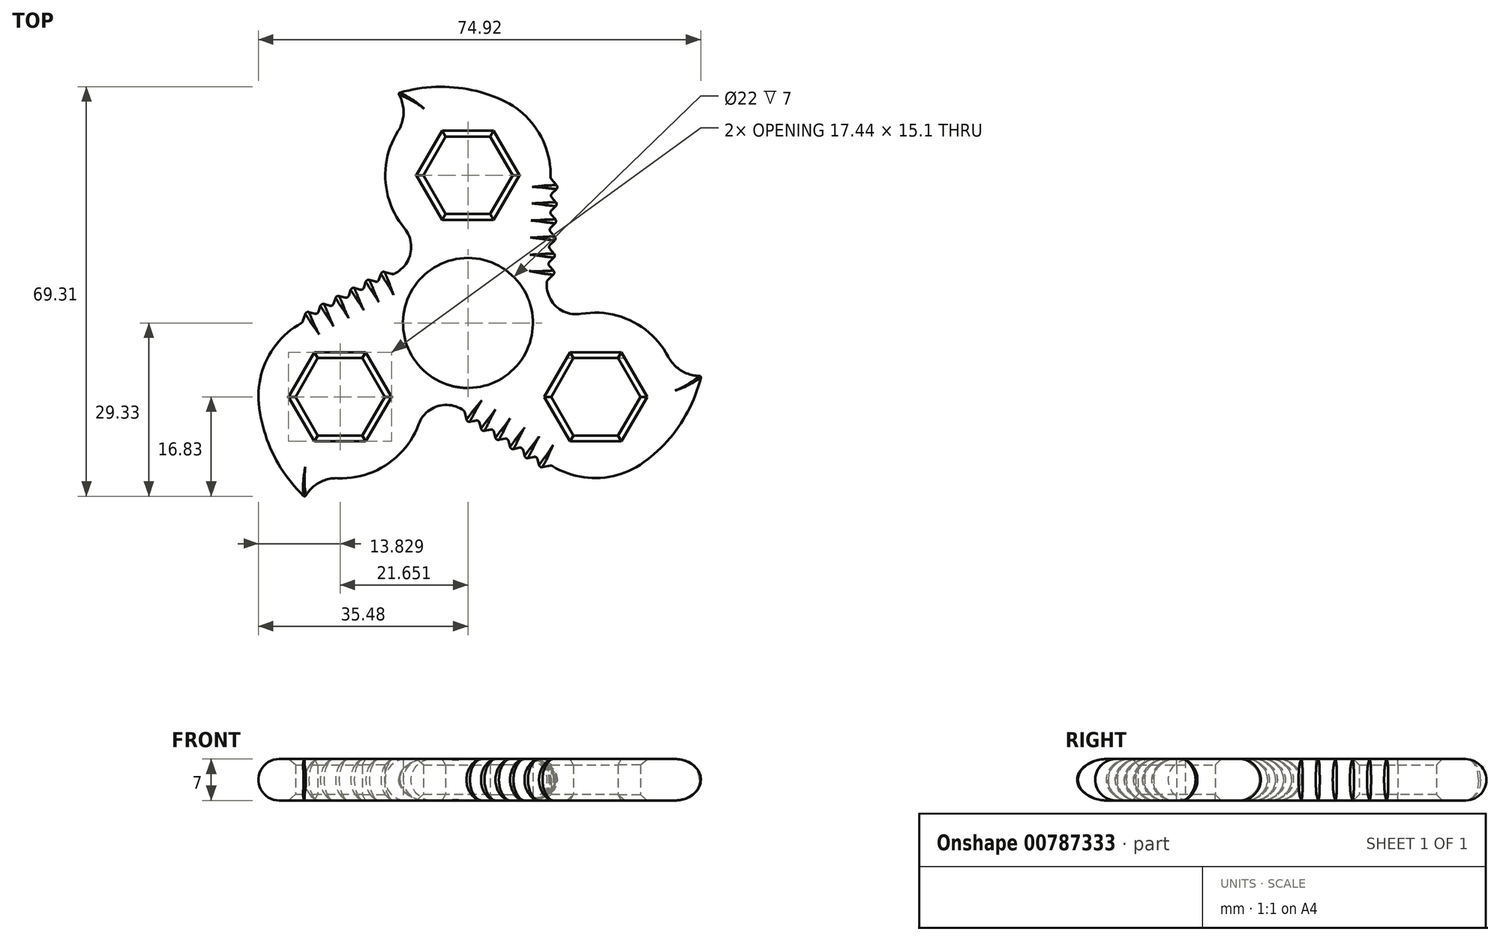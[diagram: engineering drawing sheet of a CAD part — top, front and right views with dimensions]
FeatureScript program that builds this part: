
annotation { "Feature Type Name" : "Feature", "Feature Type Description" : "" }
export const myFeature = defineFeature(function(context is Context, id is Id, definition is map)
    precondition{}
    {
        {
            var Q0;
            Q0=qCreatedBy(makeId("Top.planeOp"),FACE);
            var sketch = newSketch(context, id + "F0", { "sketchPlane" : qUnion([Q0])});
            skCircle(sketch, "E0", {"center": v(0, 0) * mm, "radius": 39 * mm, "construction": true});
            skCircle(sketch, "E1", {"center": v(0, 0) * mm, "radius": 11 * mm});
            skPoint(sketch, "E2.center", {"position": v(0.03, 0) * mm});
            skArc(sketch, "E3", {"start": v(14, 24.5) * mm, "mid": v(11.9, 32.39) * mm, "end": v(5.75, 37.77) * mm});
            skLineSegment(sketch, "E4", {"start": v(13.35, 6.66) * mm, "end": v(13.36, 7.1) * mm});
            skPoint(sketch, "E5.visualSharp", {"position": v(-4.7, 11.81) * mm});
            skArc(sketch, "E5.filletArc", {"start": v(-12.27, 8.44) * mm, "mid": v(-9.7, 11.89) * mm, "end": v(-10.77, 16.05) * mm});
            skPoint(sketch, "E6.visualSharp", {"position": v(13.05, -1.63) * mm});
            skArc(sketch, "E7", {"start": v(5.75, 37.77) * mm, "mid": v(-2.94, 39.93) * mm, "end": v(-11.83, 38.9) * mm});
            skArc(sketch, "E8", {"start": v(-11.83, 32.48) * mm, "mid": v(-10.9, 35.7) * mm, "end": v(-11.83, 38.9) * mm});
            skArc(sketch, "E9.trimOffspring", {"start": v(-11.83, 32.48) * mm, "mid": v(-13.97, 24.1) * mm, "end": v(-10.77, 16.05) * mm});
            skLineSegment(sketch, "E10", {"start": v(14, 24.5) * mm, "end": v(15.31, 23) * mm});
            skLineSegment(sketch, "E11", {"start": v(15.31, 23) * mm, "end": v(13.89, 21.6) * mm});
            skLineSegment(sketch, "E12.1.0.0", {"start": v(15.2, 20.1) * mm, "end": v(13.78, 18.7) * mm});
            skLineSegment(sketch, "E12.1.0.1", {"start": v(13.89, 21.6) * mm, "end": v(15.2, 20.1) * mm});
            skLineSegment(sketch, "E12.2.0.0", {"start": v(15.1, 17.2) * mm, "end": v(13.68, 15.8) * mm});
            skLineSegment(sketch, "E12.2.0.1", {"start": v(13.78, 18.7) * mm, "end": v(15.1, 17.2) * mm});
            skLineSegment(sketch, "E12.3.0.0", {"start": v(15, 14.3) * mm, "end": v(13.57, 12.9) * mm});
            skLineSegment(sketch, "E12.3.0.1", {"start": v(13.68, 15.8) * mm, "end": v(15, 14.3) * mm});
            skLineSegment(sketch, "E12.4.0.0", {"start": v(14.9, 11.4) * mm, "end": v(13.47, 10) * mm});
            skLineSegment(sketch, "E12.4.0.1", {"start": v(13.57, 12.9) * mm, "end": v(14.9, 11.4) * mm});
            skLineSegment(sketch, "E12.5.0.0", {"start": v(14.79, 8.5) * mm, "end": v(13.36, 7.1) * mm});
            skLineSegment(sketch, "E12.5.0.1", {"start": v(13.47, 10) * mm, "end": v(14.79, 8.5) * mm});
            skArc(sketch, "E13.1.0", {"start": v(-22.04, -26.28) * mm, "mid": v(-25.29, -27.08) * mm, "end": v(-27.6, -29.49) * mm});
            skArc(sketch, "E13.1.1", {"start": v(-1, -14.64) * mm, "mid": v(-5.27, -14.14) * mm, "end": v(-8.35, -17.14) * mm});
            skArc(sketch, "E13.1.2", {"start": v(-22.04, -26.28) * mm, "mid": v(-13.71, -23.93) * mm, "end": v(-8.35, -17.14) * mm});
            skArc(sketch, "E13.1.3", {"start": v(-35.41, -13.7) * mm, "mid": v(-32.94, -22.3) * mm, "end": v(-27.6, -29.49) * mm});
            skArc(sketch, "E13.1.4", {"start": v(-28.04, 0.08) * mm, "mid": v(-33.82, -5.68) * mm, "end": v(-35.41, -13.7) * mm});
            skLineSegment(sketch, "E13.1.6", {"start": v(-28.04, 0.08) * mm, "end": v(-27.4, 1.98) * mm});
            skLineSegment(sketch, "E13.1.7", {"start": v(-27.4, 1.98) * mm, "end": v(-25.47, 1.44) * mm});
            skLineSegment(sketch, "E13.1.8", {"start": v(-25.48, 1.44) * mm, "end": v(-24.84, 3.34) * mm});
            skLineSegment(sketch, "E13.1.9", {"start": v(-24.84, 3.34) * mm, "end": v(-22.91, 2.8) * mm});
            skLineSegment(sketch, "E13.1.10", {"start": v(-22.91, 2.8) * mm, "end": v(-22.28, 4.7) * mm});
            skLineSegment(sketch, "E13.1.11", {"start": v(-22.28, 4.7) * mm, "end": v(-20.35, 4.16) * mm});
            skLineSegment(sketch, "E13.1.12", {"start": v(-20.35, 4.16) * mm, "end": v(-19.71, 6.05) * mm});
            skLineSegment(sketch, "E13.1.13", {"start": v(-19.71, 6.05) * mm, "end": v(-17.79, 5.52) * mm});
            skLineSegment(sketch, "E13.1.14", {"start": v(-17.79, 5.51) * mm, "end": v(-17.15, 7.41) * mm});
            skLineSegment(sketch, "E13.1.15", {"start": v(-17.15, 7.41) * mm, "end": v(-15.23, 6.87) * mm});
            skLineSegment(sketch, "E13.1.16", {"start": v(-15.23, 6.87) * mm, "end": v(-14.59, 8.77) * mm});
            skLineSegment(sketch, "E13.1.17", {"start": v(-14.59, 8.77) * mm, "end": v(-12.66, 8.23) * mm});
            skLineSegment(sketch, "E13.1.18", {"start": v(-12.27, 8.44) * mm, "end": v(-12.66, 8.23) * mm});
            skArc(sketch, "E13.2.0", {"start": v(33.95, -5.74) * mm, "mid": v(36.26, -8.15) * mm, "end": v(39.5, -8.95) * mm});
            skArc(sketch, "E13.2.1", {"start": v(13.35, 6.66) * mm, "mid": v(15.05, 2.72) * mm, "end": v(19.19, 1.55) * mm});
            skArc(sketch, "E13.2.2", {"start": v(33.95, -5.74) * mm, "mid": v(27.75, 0.3) * mm, "end": v(19.19, 1.55) * mm});
            skArc(sketch, "E13.2.3", {"start": v(29.73, -23.6) * mm, "mid": v(35.95, -17.16) * mm, "end": v(39.5, -8.95) * mm});
            skArc(sketch, "E13.2.4", {"start": v(14.12, -24.11) * mm, "mid": v(22, -26.24) * mm, "end": v(29.73, -23.6) * mm});
            skLineSegment(sketch, "E13.2.6", {"start": v(14.12, -24.11) * mm, "end": v(12.16, -24.5) * mm});
            skLineSegment(sketch, "E13.2.7", {"start": v(12.16, -24.5) * mm, "end": v(11.66, -22.57) * mm});
            skLineSegment(sketch, "E13.2.8", {"start": v(11.66, -22.57) * mm, "end": v(9.7, -22.97) * mm});
            skLineSegment(sketch, "E13.2.9", {"start": v(9.7, -22.97) * mm, "end": v(9.2, -21.03) * mm});
            skLineSegment(sketch, "E13.2.10", {"start": v(9.2, -21.03) * mm, "end": v(7.24, -21.43) * mm});
            skLineSegment(sketch, "E13.2.11", {"start": v(7.24, -21.43) * mm, "end": v(6.74, -19.5) * mm});
            skLineSegment(sketch, "E13.2.12", {"start": v(6.75, -19.5) * mm, "end": v(4.79, -19.89) * mm});
            skLineSegment(sketch, "E13.2.13", {"start": v(4.79, -19.89) * mm, "end": v(4.29, -17.95) * mm});
            skLineSegment(sketch, "E13.2.14", {"start": v(4.29, -17.95) * mm, "end": v(2.33, -18.35) * mm});
            skLineSegment(sketch, "E13.2.15", {"start": v(2.33, -18.35) * mm, "end": v(1.83, -16.41) * mm});
            skLineSegment(sketch, "E13.2.16", {"start": v(1.83, -16.41) * mm, "end": v(-0.13, -16.8) * mm});
            skLineSegment(sketch, "E13.2.17", {"start": v(-0.13, -16.8) * mm, "end": v(-0.63, -14.87) * mm});
            skLineSegment(sketch, "E13.2.18", {"start": v(-1, -14.64) * mm, "end": v(-0.63, -14.87) * mm});
            skPoint(sketch, "E13.center", {"position": v(0.02, 0.15) * mm});
            skLineSegment(sketch, "E14.trimOffspring", {"start": v(-25.47, 1.44) * mm, "end": v(-25.48, 1.44) * mm});
            skLineSegment(sketch, "E15.trimOffspring", {"start": v(-22.91, 2.8) * mm, "end": v(-22.91, 2.8) * mm});
            skLineSegment(sketch, "E16.trimOffspring", {"start": v(-20.35, 4.16) * mm, "end": v(-20.35, 4.16) * mm});
            skLineSegment(sketch, "E17.trimOffspring", {"start": v(-17.79, 5.52) * mm, "end": v(-17.79, 5.51) * mm});
            skLineSegment(sketch, "E18.trimOffspring", {"start": v(-15.23, 6.87) * mm, "end": v(-15.23, 6.87) * mm});
            skLineSegment(sketch, "E19.trimOffspring", {"start": v(1.83, -16.41) * mm, "end": v(1.83, -16.41) * mm});
            skLineSegment(sketch, "E20.trimOffspring", {"start": v(4.29, -17.95) * mm, "end": v(4.29, -17.95) * mm});
            skLineSegment(sketch, "E21.trimOffspring", {"start": v(6.74, -19.5) * mm, "end": v(6.75, -19.5) * mm});
            skLineSegment(sketch, "E22.trimOffspring", {"start": v(9.2, -21.03) * mm, "end": v(9.2, -21.03) * mm});
            skLineSegment(sketch, "E23.trimOffspring", {"start": v(11.26, -22.32) * mm, "end": v(11.66, -22.57) * mm});
            skLineSegment(sketch, "E24.trimOffspring", {"start": v(13.47, 10) * mm, "end": v(13.47, 10) * mm});
            skLineSegment(sketch, "E25.trimOffspring", {"start": v(13.57, 12.9) * mm, "end": v(13.57, 12.9) * mm});
            skLineSegment(sketch, "E26.trimOffspring", {"start": v(13.68, 15.8) * mm, "end": v(13.68, 15.8) * mm});
            skLineSegment(sketch, "E27.trimOffspring", {"start": v(13.78, 18.7) * mm, "end": v(13.78, 18.7) * mm});
            skLineSegment(sketch, "E28.trimOffspring", {"start": v(13.78, 18.7) * mm, "end": v(13.78, 18.7) * mm, "construction": true});
            skLineSegment(sketch, "E29.trimOffspring", {"start": v(13.89, 21.6) * mm, "end": v(13.89, 21.6) * mm});
            skCircle(sketch, "E30.cCircle", {"center": v(0, 25) * mm, "radius": 6.55 * mm, "construction": true});
            skLineSegment(sketch, "E30.0", {"start": v(7.56, 25) * mm, "end": v(3.78, 18.45) * mm});
            skLineSegment(sketch, "E30.1", {"start": v(3.78, 18.45) * mm, "end": v(-3.78, 18.45) * mm});
            skLineSegment(sketch, "E30.2", {"start": v(-3.78, 18.45) * mm, "end": v(-7.56, 25) * mm});
            skLineSegment(sketch, "E30.3", {"start": v(-7.56, 25) * mm, "end": v(-3.78, 31.55) * mm});
            skLineSegment(sketch, "E30.4", {"start": v(-3.78, 31.55) * mm, "end": v(3.78, 31.55) * mm});
            skLineSegment(sketch, "E30.5", {"start": v(3.78, 31.55) * mm, "end": v(7.56, 25) * mm});
            skPoint(sketch, "E30.0.midPoint", {"position": v(5.67, 21.72) * mm});
            skLineSegment(sketch, "E31.1.0", {"start": v(-25.43, -19.05) * mm, "end": v(-29.21, -12.5) * mm});
            skPoint(sketch, "E31.1.1", {"position": v(-21.65, -5.95) * mm});
            skLineSegment(sketch, "E31.1.2", {"start": v(-17.87, -19.05) * mm, "end": v(-25.43, -19.05) * mm});
            skLineSegment(sketch, "E31.1.3", {"start": v(-14.09, -12.5) * mm, "end": v(-17.87, -19.05) * mm});
            skLineSegment(sketch, "E31.1.4", {"start": v(-17.87, -5.95) * mm, "end": v(-14.09, -12.5) * mm});
            skLineSegment(sketch, "E31.1.5", {"start": v(-29.21, -12.5) * mm, "end": v(-25.43, -5.95) * mm});
            skCircle(sketch, "E31.1.6", {"center": v(-21.65, -12.5) * mm, "radius": 6.55 * mm, "construction": true});
            skLineSegment(sketch, "E31.1.7", {"start": v(-25.43, -5.95) * mm, "end": v(-17.87, -5.95) * mm});
            skLineSegment(sketch, "E31.2.0", {"start": v(29.21, -12.5) * mm, "end": v(25.43, -19.05) * mm});
            skPoint(sketch, "E31.2.1", {"position": v(15.98, -15.77) * mm});
            skLineSegment(sketch, "E31.2.2", {"start": v(25.43, -5.95) * mm, "end": v(29.21, -12.5) * mm});
            skLineSegment(sketch, "E31.2.3", {"start": v(17.87, -5.95) * mm, "end": v(25.43, -5.95) * mm});
            skLineSegment(sketch, "E31.2.4", {"start": v(14.09, -12.5) * mm, "end": v(17.87, -5.95) * mm});
            skLineSegment(sketch, "E31.2.5", {"start": v(25.43, -19.05) * mm, "end": v(17.87, -19.05) * mm});
            skCircle(sketch, "E31.2.6", {"center": v(21.65, -12.5) * mm, "radius": 6.55 * mm, "construction": true});
            skLineSegment(sketch, "E31.2.7", {"start": v(17.87, -19.05) * mm, "end": v(14.09, -12.5) * mm});
            skSolve(sketch);
        }
        {
            var Q0;
            Q0=qSketchRegion(id+"F0",true);
            extrude(context, id + "F1", {"entities" : qUnion([Q0]), "depth" : 7 * mm, "offsetDistance" : 25 * mm});
        }
        {
            var Q0;
            Q0=makeQuery(id+"F1.opExtrude","SWEPT_EDGE",EDGE,{"disambiguationData":[OSD([sQuery(id+"F0.wireOp",EDGE,"E13.1.17"),sQuery(id+"F0.wireOp",EDGE,"E13.1.18")])]});
            var Q1;
            Q1=makeQuery(id+"F1.opExtrude","SWEPT_EDGE",EDGE,{"disambiguationData":[OSD([sQuery(id+"F0.wireOp",EDGE,"E13.1.16"),sQuery(id+"F0.wireOp",EDGE,"E13.1.17")])]});
            var Q2;
            Q2=makeQuery(id+"F1.opExtrude","SWEPT_EDGE",EDGE,{"disambiguationData":[OSD([sQuery(id+"F0.wireOp",EDGE,"E13.1.15"),sQuery(id+"F0.wireOp",EDGE,"E13.1.16")])]});
            var Q3;
            Q3=makeQuery(id+"F1.opExtrude","SWEPT_EDGE",EDGE,{"disambiguationData":[OSD([sQuery(id+"F0.wireOp",EDGE,"E13.1.14"),sQuery(id+"F0.wireOp",EDGE,"E13.1.15")])]});
            var Q4;
            Q4=makeQuery(id+"F1.opExtrude","SWEPT_EDGE",EDGE,{"disambiguationData":[OSD([sQuery(id+"F0.wireOp",EDGE,"E13.1.13"),sQuery(id+"F0.wireOp",EDGE,"E13.1.14")])]});
            var Q5;
            Q5=makeQuery(id+"F1.opExtrude","SWEPT_EDGE",EDGE,{"disambiguationData":[OSD([sQuery(id+"F0.wireOp",EDGE,"E13.1.12"),sQuery(id+"F0.wireOp",EDGE,"E13.1.13")])]});
            var Q6;
            Q6=makeQuery(id+"F1.opExtrude","SWEPT_EDGE",EDGE,{"disambiguationData":[OSD([sQuery(id+"F0.wireOp",EDGE,"E13.1.11"),sQuery(id+"F0.wireOp",EDGE,"E13.1.12")])]});
            var Q7;
            Q7=makeQuery(id+"F1.opExtrude","SWEPT_EDGE",EDGE,{"disambiguationData":[OSD([sQuery(id+"F0.wireOp",EDGE,"E13.1.10"),sQuery(id+"F0.wireOp",EDGE,"E13.1.11")])]});
            var Q8;
            Q8=makeQuery(id+"F1.opExtrude","SWEPT_EDGE",EDGE,{"disambiguationData":[OSD([sQuery(id+"F0.wireOp",EDGE,"E13.1.9"),sQuery(id+"F0.wireOp",EDGE,"E13.1.10")])]});
            var Q9;
            Q9=makeQuery(id+"F1.opExtrude","SWEPT_EDGE",EDGE,{"disambiguationData":[OSD([sQuery(id+"F0.wireOp",EDGE,"E13.1.8"),sQuery(id+"F0.wireOp",EDGE,"E13.1.9")])]});
            var Q10;
            Q10=makeQuery(id+"F1.opExtrude","SWEPT_EDGE",EDGE,{"disambiguationData":[OSD([sQuery(id+"F0.wireOp",EDGE,"E13.1.7"),sQuery(id+"F0.wireOp",EDGE,"E13.1.8")])]});
            var Q11;
            Q11=makeQuery(id+"F1.opExtrude","SWEPT_EDGE",EDGE,{"disambiguationData":[OSD([sQuery(id+"F0.wireOp",EDGE,"E13.1.6"),sQuery(id+"F0.wireOp",EDGE,"E13.1.7")])]});
            var Q12;
            Q12=makeQuery(id+"F1.opExtrude","SWEPT_EDGE",EDGE,{"disambiguationData":[OSD([sQuery(id+"F0.wireOp",EDGE,"E13.1.4"),sQuery(id+"F0.wireOp",EDGE,"E13.1.6")])]});
            var Q13;
            Q13=makeQuery(id+"F1.opExtrude","SWEPT_EDGE",EDGE,{"disambiguationData":[OSD([sQuery(id+"F0.wireOp",EDGE,"E13.2.17"),sQuery(id+"F0.wireOp",EDGE,"E13.2.18")])]});
            var Q14;
            Q14=makeQuery(id+"F1.opExtrude","SWEPT_EDGE",EDGE,{"disambiguationData":[OSD([sQuery(id+"F0.wireOp",EDGE,"E13.2.16"),sQuery(id+"F0.wireOp",EDGE,"E13.2.17")])]});
            var Q15;
            Q15=makeQuery(id+"F1.opExtrude","SWEPT_EDGE",EDGE,{"disambiguationData":[OSD([sQuery(id+"F0.wireOp",EDGE,"E13.2.15"),sQuery(id+"F0.wireOp",EDGE,"E13.2.16")])]});
            var Q16;
            Q16=makeQuery(id+"F1.opExtrude","SWEPT_EDGE",EDGE,{"disambiguationData":[OSD([sQuery(id+"F0.wireOp",EDGE,"E13.2.14"),sQuery(id+"F0.wireOp",EDGE,"E13.2.15")])]});
            var Q17;
            Q17=makeQuery(id+"F1.opExtrude","SWEPT_EDGE",EDGE,{"disambiguationData":[OSD([sQuery(id+"F0.wireOp",EDGE,"E13.2.13"),sQuery(id+"F0.wireOp",EDGE,"E13.2.14")])]});
            var Q18;
            Q18=makeQuery(id+"F1.opExtrude","SWEPT_EDGE",EDGE,{"disambiguationData":[OSD([sQuery(id+"F0.wireOp",EDGE,"E13.2.12"),sQuery(id+"F0.wireOp",EDGE,"E13.2.13")])]});
            var Q19;
            Q19=makeQuery(id+"F1.opExtrude","SWEPT_EDGE",EDGE,{"disambiguationData":[OSD([sQuery(id+"F0.wireOp",EDGE,"E13.2.11"),sQuery(id+"F0.wireOp",EDGE,"E13.2.12")])]});
            var Q20;
            Q20=makeQuery(id+"F1.opExtrude","SWEPT_EDGE",EDGE,{"disambiguationData":[OSD([sQuery(id+"F0.wireOp",EDGE,"E13.2.10"),sQuery(id+"F0.wireOp",EDGE,"E13.2.11")])]});
            var Q21;
            Q21=makeQuery(id+"F1.opExtrude","SWEPT_EDGE",EDGE,{"disambiguationData":[OSD([sQuery(id+"F0.wireOp",EDGE,"E13.2.9"),sQuery(id+"F0.wireOp",EDGE,"E13.2.10")])]});
            var Q22;
            Q22=makeQuery(id+"F1.opExtrude","SWEPT_EDGE",EDGE,{"disambiguationData":[OSD([sQuery(id+"F0.wireOp",EDGE,"E13.2.8"),sQuery(id+"F0.wireOp",EDGE,"E13.2.9")])]});
            var Q23;
            Q23=makeQuery(id+"F1.opExtrude","SWEPT_EDGE",EDGE,{"disambiguationData":[OSD([sQuery(id+"F0.wireOp",EDGE,"E13.2.7"),sQuery(id+"F0.wireOp",EDGE,"E13.2.8")])]});
            var Q24;
            Q24=makeQuery(id+"F1.opExtrude","SWEPT_EDGE",EDGE,{"disambiguationData":[OSD([sQuery(id+"F0.wireOp",EDGE,"E13.2.6"),sQuery(id+"F0.wireOp",EDGE,"E13.2.7")])]});
            var Q25;
            Q25=makeQuery(id+"F1.opExtrude","SWEPT_EDGE",EDGE,{"disambiguationData":[OSD([sQuery(id+"F0.wireOp",EDGE,"E13.2.4"),sQuery(id+"F0.wireOp",EDGE,"E13.2.6")])]});
            var Q26;
            Q26=makeQuery(id+"F1.opExtrude","SWEPT_EDGE",EDGE,{"disambiguationData":[OSD([sQuery(id+"F0.wireOp",EDGE,"E3"),sQuery(id+"F0.wireOp",EDGE,"E10")])]});
            var Q27;
            Q27=makeQuery(id+"F1.opExtrude","SWEPT_EDGE",EDGE,{"disambiguationData":[OSD([sQuery(id+"F0.wireOp",EDGE,"E10"),sQuery(id+"F0.wireOp",EDGE,"E11")])]});
            var Q28;
            Q28=makeQuery(id+"F1.opExtrude","SWEPT_EDGE",EDGE,{"disambiguationData":[OSD([sQuery(id+"F0.wireOp",EDGE,"E11"),sQuery(id+"F0.wireOp",EDGE,"E12.1.0.1")])]});
            var Q29;
            Q29=makeQuery(id+"F1.opExtrude","SWEPT_EDGE",EDGE,{"disambiguationData":[OSD([sQuery(id+"F0.wireOp",EDGE,"E12.1.0.0"),sQuery(id+"F0.wireOp",EDGE,"E12.1.0.1")])]});
            var Q30;
            Q30=makeQuery(id+"F1.opExtrude","SWEPT_EDGE",EDGE,{"disambiguationData":[OSD([sQuery(id+"F0.wireOp",EDGE,"E12.1.0.0"),sQuery(id+"F0.wireOp",EDGE,"E12.2.0.1")])]});
            var Q31;
            Q31=makeQuery(id+"F1.opExtrude","SWEPT_EDGE",EDGE,{"disambiguationData":[OSD([sQuery(id+"F0.wireOp",EDGE,"E12.2.0.0"),sQuery(id+"F0.wireOp",EDGE,"E12.2.0.1")])]});
            var Q32;
            Q32=makeQuery(id+"F1.opExtrude","SWEPT_EDGE",EDGE,{"disambiguationData":[OSD([sQuery(id+"F0.wireOp",EDGE,"E12.2.0.0"),sQuery(id+"F0.wireOp",EDGE,"E12.3.0.1")])]});
            var Q33;
            Q33=makeQuery(id+"F1.opExtrude","SWEPT_EDGE",EDGE,{"disambiguationData":[OSD([sQuery(id+"F0.wireOp",EDGE,"E12.3.0.0"),sQuery(id+"F0.wireOp",EDGE,"E12.3.0.1")])]});
            var Q34;
            Q34=makeQuery(id+"F1.opExtrude","SWEPT_EDGE",EDGE,{"disambiguationData":[OSD([sQuery(id+"F0.wireOp",EDGE,"E12.3.0.0"),sQuery(id+"F0.wireOp",EDGE,"E12.4.0.1")])]});
            var Q35;
            Q35=makeQuery(id+"F1.opExtrude","SWEPT_EDGE",EDGE,{"disambiguationData":[OSD([sQuery(id+"F0.wireOp",EDGE,"E12.4.0.0"),sQuery(id+"F0.wireOp",EDGE,"E12.4.0.1")])]});
            var Q36;
            Q36=makeQuery(id+"F1.opExtrude","SWEPT_EDGE",EDGE,{"disambiguationData":[OSD([sQuery(id+"F0.wireOp",EDGE,"E12.4.0.0"),sQuery(id+"F0.wireOp",EDGE,"E12.5.0.1")])]});
            var Q37;
            Q37=makeQuery(id+"F1.opExtrude","SWEPT_EDGE",EDGE,{"disambiguationData":[OSD([sQuery(id+"F0.wireOp",EDGE,"E12.5.0.0"),sQuery(id+"F0.wireOp",EDGE,"E12.5.0.1")])]});
            var Q38;
            Q38=makeQuery(id+"F1.opExtrude","SWEPT_EDGE",EDGE,{"disambiguationData":[OSD([sQuery(id+"F0.wireOp",EDGE,"E4"),sQuery(id+"F0.wireOp",EDGE,"E12.5.0.0")])]});
            fillet(context, id + "F2", {"entities" : qUnion([Q0, Q1, Q2, Q3, Q4, Q5, Q6, Q7, Q8, Q9, Q10, Q11, Q12, Q13, Q14, Q15, Q16, Q17, Q18, Q19, Q20, Q21, Q22, Q23, Q24, Q25, Q26, Q27, Q28, Q29, Q30, Q31, Q32, Q33, Q34, Q35, Q36, Q37, Q38]), "radius" : .5 * mm, "tangentPropagation" : true, "allowEdgeOverflow" : false});
        }
        {
            var Q0;
            Q0=makeQuery(id+"F1.opExtrude","SWEPT_EDGE",EDGE,{"disambiguationData":[OSD([sQuery(id+"F0.wireOp",EDGE,"E7"),sQuery(id+"F0.wireOp",EDGE,"E8")])]});
            var Q1;
            Q1=makeQuery(id+"F1.opExtrude","SWEPT_EDGE",EDGE,{"disambiguationData":[OSD([sQuery(id+"F0.wireOp",EDGE,"E13.1.0"),sQuery(id+"F0.wireOp",EDGE,"E13.1.3")])]});
            var Q2;
            Q2=makeQuery(id+"F1.opExtrude","SWEPT_EDGE",EDGE,{"disambiguationData":[OSD([sQuery(id+"F0.wireOp",EDGE,"E13.2.0"),sQuery(id+"F0.wireOp",EDGE,"E13.2.3")])]});
            fillet(context, id + "F3", {"entities" : qUnion([Q0, Q1, Q2]), "radius" : .25 * mm, "tangentPropagation" : true, "allowEdgeOverflow" : false});
        }
        {
            var Q0;
            Q0=makeQuery(id+"F1.opExtrude","CAP_EDGE",EDGE,{"disambiguationData":[OSD([sQuery(id+"F0.wireOp",EDGE,"E13.2.4")])],"isStart":false});
            var Q1;
            Q1=makeQuery(id+"F1.opExtrude","CAP_EDGE",EDGE,{"disambiguationData":[OSD([sQuery(id+"F0.wireOp",EDGE,"E13.1.1")])],"isStart":true});
            fillet(context, id + "F4", {"entities" : qUnion([Q0, Q1]), "radius" : 3.5 * mm, "tangentPropagation" : true, "allowEdgeOverflow" : false});
        }
        {
            var Q0;
            Q0=makeQuery(id+"F1.opExtrude","CAP_EDGE",EDGE,{"disambiguationData":[OSD([sQuery(id+"F0.wireOp",EDGE,"E31.1.5")])],"isStart":false});
            var Q1;
            Q1=makeQuery(id+"F1.opExtrude","CAP_EDGE",EDGE,{"disambiguationData":[OSD([sQuery(id+"F0.wireOp",EDGE,"E31.1.7")])],"isStart":false});
            var Q2;
            Q2=makeQuery(id+"F1.opExtrude","CAP_EDGE",EDGE,{"disambiguationData":[OSD([sQuery(id+"F0.wireOp",EDGE,"E31.1.4")])],"isStart":false});
            var Q3;
            Q3=makeQuery(id+"F1.opExtrude","CAP_EDGE",EDGE,{"disambiguationData":[OSD([sQuery(id+"F0.wireOp",EDGE,"E31.1.3")])],"isStart":false});
            var Q4;
            Q4=makeQuery(id+"F1.opExtrude","CAP_EDGE",EDGE,{"disambiguationData":[OSD([sQuery(id+"F0.wireOp",EDGE,"E31.1.2")])],"isStart":false});
            var Q5;
            Q5=makeQuery(id+"F1.opExtrude","CAP_EDGE",EDGE,{"disambiguationData":[OSD([sQuery(id+"F0.wireOp",EDGE,"E31.1.0")])],"isStart":false});
            var Q6;
            Q6=makeQuery(id+"F1.opExtrude","CAP_EDGE",EDGE,{"disambiguationData":[OSD([sQuery(id+"F0.wireOp",EDGE,"E31.2.7")])],"isStart":false});
            var Q7;
            Q7=makeQuery(id+"F1.opExtrude","CAP_EDGE",EDGE,{"disambiguationData":[OSD([sQuery(id+"F0.wireOp",EDGE,"E31.2.5")])],"isStart":false});
            var Q8;
            Q8=makeQuery(id+"F1.opExtrude","CAP_EDGE",EDGE,{"disambiguationData":[OSD([sQuery(id+"F0.wireOp",EDGE,"E31.2.0")])],"isStart":false});
            var Q9;
            Q9=makeQuery(id+"F1.opExtrude","CAP_EDGE",EDGE,{"disambiguationData":[OSD([sQuery(id+"F0.wireOp",EDGE,"E31.2.2")])],"isStart":false});
            var Q10;
            Q10=makeQuery(id+"F1.opExtrude","CAP_EDGE",EDGE,{"disambiguationData":[OSD([sQuery(id+"F0.wireOp",EDGE,"E31.2.3")])],"isStart":false});
            var Q11;
            Q11=makeQuery(id+"F1.opExtrude","CAP_EDGE",EDGE,{"disambiguationData":[OSD([sQuery(id+"F0.wireOp",EDGE,"E31.2.4")])],"isStart":false});
            var Q12;
            Q12=makeQuery(id+"F1.opExtrude","CAP_EDGE",EDGE,{"disambiguationData":[OSD([sQuery(id+"F0.wireOp",EDGE,"E31.2.4")])],"isStart":true});
            var Q13;
            Q13=makeQuery(id+"F1.opExtrude","CAP_EDGE",EDGE,{"disambiguationData":[OSD([sQuery(id+"F0.wireOp",EDGE,"E31.2.7")])],"isStart":true});
            var Q14;
            Q14=makeQuery(id+"F1.opExtrude","CAP_EDGE",EDGE,{"disambiguationData":[OSD([sQuery(id+"F0.wireOp",EDGE,"E31.2.5")])],"isStart":true});
            var Q15;
            Q15=makeQuery(id+"F1.opExtrude","CAP_EDGE",EDGE,{"disambiguationData":[OSD([sQuery(id+"F0.wireOp",EDGE,"E31.2.0")])],"isStart":true});
            var Q16;
            Q16=makeQuery(id+"F1.opExtrude","CAP_EDGE",EDGE,{"disambiguationData":[OSD([sQuery(id+"F0.wireOp",EDGE,"E31.2.2")])],"isStart":true});
            var Q17;
            Q17=makeQuery(id+"F1.opExtrude","CAP_EDGE",EDGE,{"disambiguationData":[OSD([sQuery(id+"F0.wireOp",EDGE,"E31.1.4")])],"isStart":true});
            var Q18;
            Q18=makeQuery(id+"F1.opExtrude","CAP_EDGE",EDGE,{"disambiguationData":[OSD([sQuery(id+"F0.wireOp",EDGE,"E31.1.3")])],"isStart":true});
            var Q19;
            Q19=makeQuery(id+"F1.opExtrude","CAP_EDGE",EDGE,{"disambiguationData":[OSD([sQuery(id+"F0.wireOp",EDGE,"E31.1.2")])],"isStart":true});
            var Q20;
            Q20=makeQuery(id+"F1.opExtrude","CAP_EDGE",EDGE,{"disambiguationData":[OSD([sQuery(id+"F0.wireOp",EDGE,"E31.1.0")])],"isStart":true});
            var Q21;
            Q21=makeQuery(id+"F1.opExtrude","CAP_EDGE",EDGE,{"disambiguationData":[OSD([sQuery(id+"F0.wireOp",EDGE,"E31.1.5")])],"isStart":true});
            var Q22;
            Q22=makeQuery(id+"F1.opExtrude","CAP_EDGE",EDGE,{"disambiguationData":[OSD([sQuery(id+"F0.wireOp",EDGE,"E31.1.7")])],"isStart":true});
            var Q23;
            Q23=makeQuery(id+"F1.opExtrude","CAP_EDGE",EDGE,{"disambiguationData":[OSD([sQuery(id+"F0.wireOp",EDGE,"E30.0")])],"isStart":true});
            var Q24;
            Q24=makeQuery(id+"F1.opExtrude","CAP_EDGE",EDGE,{"disambiguationData":[OSD([sQuery(id+"F0.wireOp",EDGE,"E30.5")])],"isStart":true});
            var Q25;
            Q25=makeQuery(id+"F1.opExtrude","CAP_EDGE",EDGE,{"disambiguationData":[OSD([sQuery(id+"F0.wireOp",EDGE,"E30.4")])],"isStart":true});
            var Q26;
            Q26=makeQuery(id+"F1.opExtrude","CAP_EDGE",EDGE,{"disambiguationData":[OSD([sQuery(id+"F0.wireOp",EDGE,"E30.3")])],"isStart":true});
            var Q27;
            Q27=makeQuery(id+"F1.opExtrude","CAP_EDGE",EDGE,{"disambiguationData":[OSD([sQuery(id+"F0.wireOp",EDGE,"E30.2")])],"isStart":true});
            var Q28;
            Q28=makeQuery(id+"F1.opExtrude","CAP_EDGE",EDGE,{"disambiguationData":[OSD([sQuery(id+"F0.wireOp",EDGE,"E30.1")])],"isStart":true});
            var Q29;
            Q29=makeQuery(id+"F1.opExtrude","CAP_EDGE",EDGE,{"disambiguationData":[OSD([sQuery(id+"F0.wireOp",EDGE,"E30.4")])],"isStart":false});
            var Q30;
            Q30=makeQuery(id+"F1.opExtrude","CAP_EDGE",EDGE,{"disambiguationData":[OSD([sQuery(id+"F0.wireOp",EDGE,"E30.3")])],"isStart":false});
            var Q31;
            Q31=makeQuery(id+"F1.opExtrude","CAP_EDGE",EDGE,{"disambiguationData":[OSD([sQuery(id+"F0.wireOp",EDGE,"E30.2")])],"isStart":false});
            var Q32;
            Q32=makeQuery(id+"F1.opExtrude","CAP_EDGE",EDGE,{"disambiguationData":[OSD([sQuery(id+"F0.wireOp",EDGE,"E30.1")])],"isStart":false});
            var Q33;
            Q33=makeQuery(id+"F1.opExtrude","CAP_EDGE",EDGE,{"disambiguationData":[OSD([sQuery(id+"F0.wireOp",EDGE,"E30.0")])],"isStart":false});
            var Q34;
            Q34=makeQuery(id+"F1.opExtrude","CAP_EDGE",EDGE,{"disambiguationData":[OSD([sQuery(id+"F0.wireOp",EDGE,"E30.5")])],"isStart":false});
            chamfer(context, id + "F5", {"entities" : qUnion([Q0, Q1, Q2, Q3, Q4, Q5, Q6, Q7, Q8, Q9, Q10, Q11, Q12, Q13, Q14, Q15, Q16, Q17, Q18, Q19, Q20, Q21, Q22, Q23, Q24, Q25, Q26, Q27, Q28, Q29, Q30, Q31, Q32, Q33, Q34]), "width" : 1 * mm, "tangentPropagation" : true});
        }
    });
